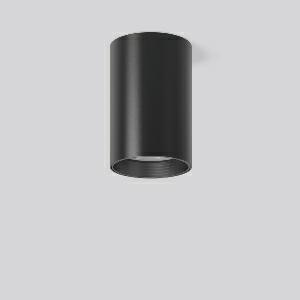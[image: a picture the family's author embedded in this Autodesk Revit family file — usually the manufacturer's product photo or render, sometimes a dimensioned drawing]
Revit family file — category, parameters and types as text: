
# Revit family: heledon_maxi_a_931234_003_76_2a4d
name_source: partatom
category: Lighting Fixtures
units: mm (PartAtom-declared; Revit-internal decimal feet)

## family parameters
Cut with Voids When Loaded = No
Host = Face
Light Source = No
Part Type = Normal
Room Calculation Point = No
Round Connector Dimension = Use Diameter
Shared = No

## types (1)
- HELEDON maxi A (1 x LED Modul 932 fresh meat, 1800 lm, 3200)
    Apparent Load = 33 VA
    Approval mark = CE
    CIE Flux Codes = 97 100 100 100 100
    Color Rendering = 90
    Color Temperature = 3200
    Default Elevation = 1800 mm  [stored 5.90551 ft]
    Description = Series: HELEDON maxi
Cylindrical surface-mounted downlight. Housing: die-cast aluminium, powder-coated. Internal ceiling frame polycarbonate with bayonet mounting. Black plastic ring and recessed LED to prevent glare from the side. Optical assembly with lens made of plastic (polycarbonate) for the best homogeneous light distribution - can be changed without tools. Special LED for illumination of meat included. Suitable for Ceiling mounting. Easy installation with a separate ceiling frame with bayonet mounting and plug connection. Driver integrated. Connected via plug-in connector. High quality converter without flickering and stroboscopic effect. The following accessories can be mounted without use of tools: interchangeable lenses, decorative glasses, honeycomb louvre, clear and frosted diffusers, white interchangeable plastic ring. 
Colour: deep black, matt (RAL 9005)
Diameter: 123 mm
Height: 183 mm
Lamp: LED
Socket: without socket
Colour temperature: fresh meat
System power: 33 W
Rated luminous flux: 1800 lm
Luminous efficiency: 55 lm/W
Control gear: Converter, dimmable, DALI
Protection class: I
Type of protection: IP 20
    Height = 183 mm
    Lamp = 1 x LED Modul 932 fresh meat
    Lamp Light Flux = 1800 lm
    Lamp count = 1
    Length = 123 mm
    Lifetime = 50000 h
    Luminous efficacy = 55 lm/W
    Manufacturer = RZB
    ModVariant = No
    Model = 931234.003.76
    Mounting Place = Ceiling
    Mounting Type = Surface mounted
    Number of Poles = 1
    OnlyDefault = Yes
    Power Factor = 1
    Product Name = HELEDON maxi A
    Product group = Surface mounted downlights
    ProductGroupID = 302
    Protection Class = Protection class I
    Protection Degree = IP 20
    RLX_Detail_Level = 1
    RLX_Emergency_Light_Flux = 0 lm
    RLX_Emergency_Type = 0
    RLX_Emergency_Type_DB = No
    RlxData = <blob elided: 97585 chars, md5=5935a792>
    Socket = socket
    Standby Power = 0 W
    System Light Flux = 1800 lm
    System Power = 33 W
    Type Comments = Product without accessories
    Type Image = 931193.003.jpg
    URL = http://relux.com
    VarID = ---
    Voltage = 230 V
    Voltage Range = 220-240 V
    Weight = 0.00 kg
    Width = 0 mm  [stored 0 ft]

note: [stored X ft] marks values corroborated as IEEE doubles in the binary element streams (Revit-internal decimal feet)

## geometry (parser evidence)
native form markers: Blend x4, Sweep x11
no freeform markers — native parametric forms only
